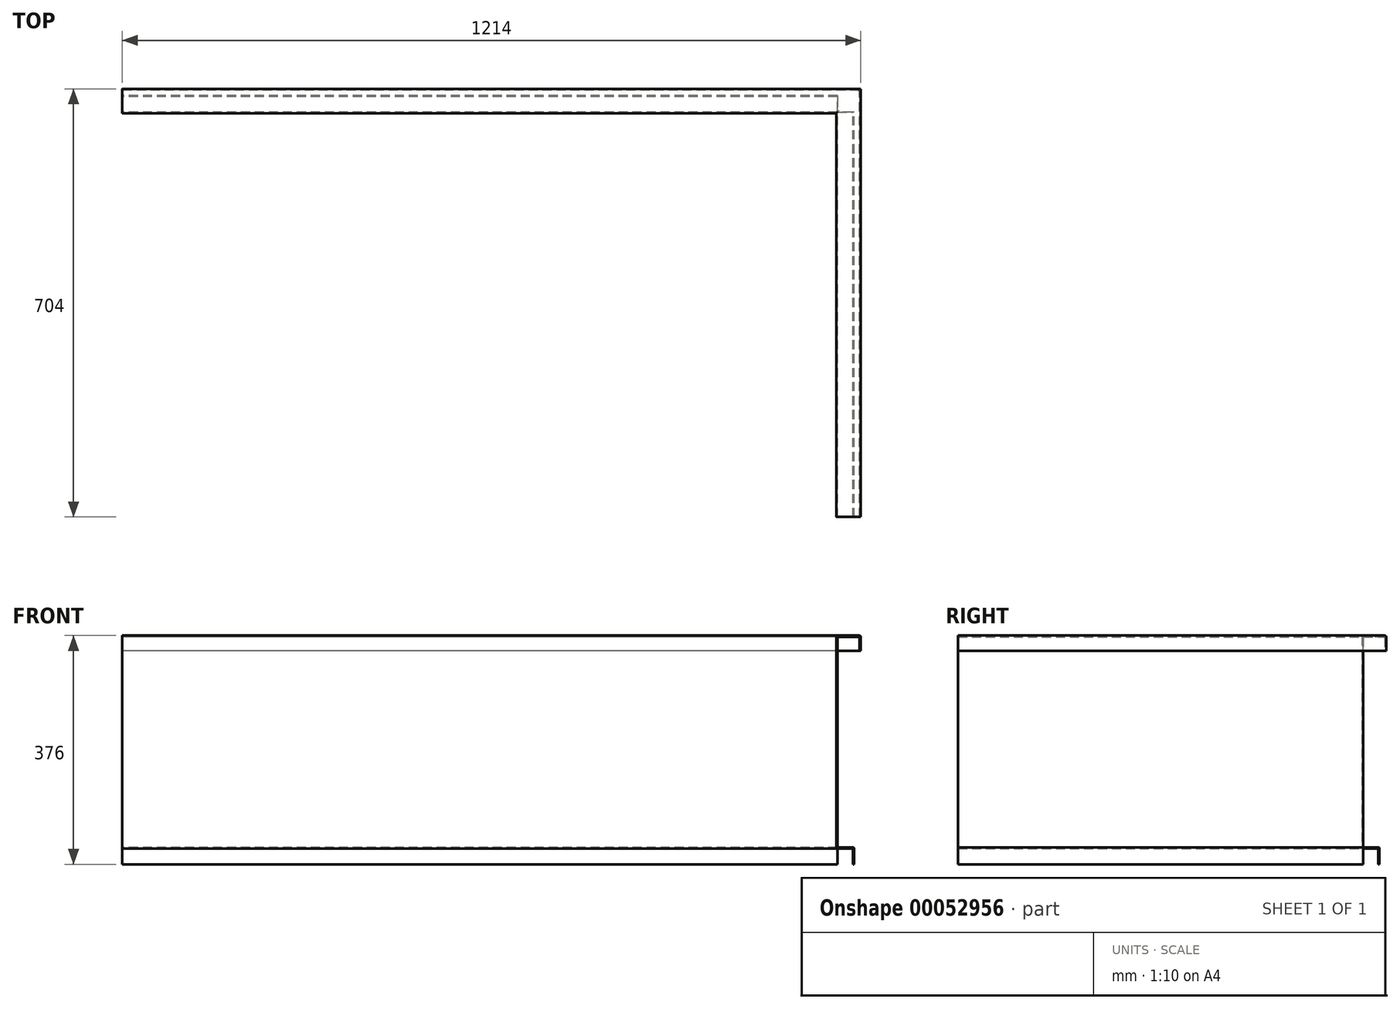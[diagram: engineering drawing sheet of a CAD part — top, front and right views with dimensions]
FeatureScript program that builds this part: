
annotation { "Feature Type Name" : "Feature", "Feature Type Description" : "" }
export const myFeature = defineFeature(function(context is Context, id is Id, definition is map)
    precondition{}
    {
        {
            var Q0;
            Q0=qCreatedBy(makeId("Front.planeOp"),FACE);
            var sketch = newSketch(context, id + "F0", { "sketchPlane" : qUnion([Q0])});
            skLineSegment(sketch, "E0", {"start": v(38, -25) * mm, "end": v(38, -2) * mm});
            skLineSegment(sketch, "E1", {"start": v(38, -2) * mm, "end": v(2, -2) * mm});
            skLineSegment(sketch, "E2", {"start": v(2, -2) * mm, "end": v(2, -348) * mm});
            skLineSegment(sketch, "E3", {"start": v(2, -348) * mm, "end": v(29, -348) * mm});
            skLineSegment(sketch, "E4", {"start": v(29, -348) * mm, "end": v(29, -376) * mm});
            skLineSegment(sketch, "E5.0", {"start": v(27, -350) * mm, "end": v(27, -376) * mm});
            skLineSegment(sketch, "E5.1", {"start": v(40, -25) * mm, "end": v(40, 0) * mm});
            skLineSegment(sketch, "E5.2", {"start": v(40, 0) * mm, "end": v(0, 0) * mm});
            skLineSegment(sketch, "E5.3", {"start": v(0, 0) * mm, "end": v(0, -350) * mm});
            skLineSegment(sketch, "E5.4", {"start": v(0, -350) * mm, "end": v(27, -350) * mm});
            skLineSegment(sketch, "E6", {"start": v(27, -376) * mm, "end": v(29, -376) * mm});
            skLineSegment(sketch, "E7", {"start": v(38, -25) * mm, "end": v(40, -25) * mm});
            skSolve(sketch);
        }
        {
            var Q0;
            Q0=qCreatedBy(makeId("Top.planeOp"),FACE);
            var sketch = newSketch(context, id + "F1", { "sketchPlane" : qUnion([Q0])});
            skLineSegment(sketch, "E8", {"start": v(0, 0) * mm, "end": v(0, 664) * mm});
            skLineSegment(sketch, "E9", {"start": v(0, 664) * mm, "end": v(-1174, 664) * mm});
            skSolve(sketch);
        }
        {
            var Q0;
            Q0 = qSketchRegion(id + "F0", true);
            var Q1;
            Q1 = qConstructionFilter(qBodyType(qCreatedBy(id + "F1" ,EDGE), BodyType.WIRE), ConstructionObject.NO);
            sweep(context, id + "F2", {"profiles" : qUnion([Q0]), "path" : qUnion([Q1])});
        }
        {
            var Q0;
            Q0=makeQuery(id+"F2.opSweep","SWEPT_FACE",FACE,{"disambiguationData":[OSD([sQuery(id+"F0.wireOp",EDGE,"E3"),sQuery(id+"F1.wireOp",EDGE,"E8")])]});
            var sketch = newSketch(context, id + "F3", { "sketchPlane" : qUnion([Q0])});
            skLineSegment(sketch, "E10.bottom", {"start": v(2, 666) * mm, "end": v(29, 666) * mm});
            skLineSegment(sketch, "E10.top", {"start": v(2, 693) * mm, "end": v(29, 693) * mm});
            skLineSegment(sketch, "E10.left", {"start": v(2, 666) * mm, "end": v(2, 693) * mm});
            skLineSegment(sketch, "E10.right", {"start": v(29, 666) * mm, "end": v(29, 693) * mm});
            skSolve(sketch);
        }
        {
            var Q0;
            Q0 = qSketchRegion(id + "F3", true);
            extrude(context, id + "F4", {"entities" : qUnion([Q0]), "operationType" : NewBodyOperationType.REMOVE, "oppositeDirection" : true, "depth" : 30 * mm});
        }
        {
            var Q0;
            Q0=makeQuery(id+"F2.opSweep","SWEPT_EDGE",EDGE,{"disambiguationData":[OSD([sQuery(id+"F0.wireOp",EDGE,"E3"),sQuery(id+"F0.wireOp",EDGE,"E4"),sQuery(id+"F1.wireOp",EDGE,"E9")])]});
            var Q1;
            Q1=makeQuery(id+"F2.opSweep","SWEPT_EDGE",EDGE,{"disambiguationData":[OSD([sQuery(id+"F0.wireOp",EDGE,"E2"),sQuery(id+"F0.wireOp",EDGE,"E3"),sQuery(id+"F1.wireOp",EDGE,"E9")])]});
            var Q2;
            Q2=makeQuery(id+"F2.opSweep","SWEPT_EDGE",EDGE,{"disambiguationData":[OSD([sQuery(id+"F0.wireOp",EDGE,"E5.1"),sQuery(id+"F0.wireOp",EDGE,"E5.2"),sQuery(id+"F1.wireOp",EDGE,"E9")])]});
            var Q3;
            Q3=makeQuery(id+"F2.opSweep","SWEPT_EDGE",EDGE,{"disambiguationData":[OSD([sQuery(id+"F0.wireOp",EDGE,"E5.2"),sQuery(id+"F0.wireOp",EDGE,"E5.3"),sQuery(id+"F1.wireOp",EDGE,"E9")])]});
            var Q4;
            Q4=makeQuery(id+"F2.opSweep","SWEPT_EDGE",EDGE,{"disambiguationData":[OSD([sQuery(id+"F0.wireOp",EDGE,"E5.3"),sQuery(id+"F0.wireOp",EDGE,"E5.4"),sQuery(id+"F1.wireOp",EDGE,"E9")])]});
            var Q5;
            Q5=makeQuery(id+"F2.opSweep","SWEPT_EDGE",EDGE,{"disambiguationData":[OSD([sQuery(id+"F0.wireOp",EDGE,"E5.0"),sQuery(id+"F0.wireOp",EDGE,"E5.4"),sQuery(id+"F1.wireOp",EDGE,"E9")])]});
            var Q6;
            Q6=makeQuery(id+"F2.opSweep","SWEPT_EDGE",EDGE,{"disambiguationData":[OSD([sQuery(id+"F0.wireOp",EDGE,"E1"),sQuery(id+"F0.wireOp",EDGE,"E2"),sQuery(id+"F1.wireOp",EDGE,"E9")])]});
            var Q7;
            Q7=makeQuery(id+"F2.opSweep","SWEPT_EDGE",EDGE,{"disambiguationData":[OSD([sQuery(id+"F0.wireOp",EDGE,"E0"),sQuery(id+"F0.wireOp",EDGE,"E1"),sQuery(id+"F1.wireOp",EDGE,"E9")])]});
            var Q8;
            Q8=makeQuery(id+"F2.opSweep","SWEPT_EDGE",EDGE,{"disambiguationData":[OSD([sQuery(id+"F0.wireOp",EDGE,"E5.1"),sQuery(id+"F0.wireOp",EDGE,"E5.2"),sQuery(id+"F1.wireOp",EDGE,"E8")])]});
            var Q9;
            Q9=makeQuery(id+"F2.opSweep","SWEPT_EDGE",EDGE,{"disambiguationData":[OSD([sQuery(id+"F0.wireOp",EDGE,"E5.2"),sQuery(id+"F0.wireOp",EDGE,"E5.3"),sQuery(id+"F1.wireOp",EDGE,"E8")])]});
            var Q10;
            Q10=makeQuery(id+"F2.opSweep","SWEPT_EDGE",EDGE,{"disambiguationData":[OSD([sQuery(id+"F0.wireOp",EDGE,"E5.3"),sQuery(id+"F0.wireOp",EDGE,"E5.4"),sQuery(id+"F1.wireOp",EDGE,"E8")])]});
            var Q11;
            Q11=makeQuery(id+"F2.opSweep","SWEPT_EDGE",EDGE,{"disambiguationData":[OSD([sQuery(id+"F0.wireOp",EDGE,"E5.0"),sQuery(id+"F0.wireOp",EDGE,"E5.4"),sQuery(id+"F1.wireOp",EDGE,"E8")])]});
            var Q12;
            Q12=makeQuery(id+"F2.opSweep","SWEPT_EDGE",EDGE,{"disambiguationData":[OSD([sQuery(id+"F0.wireOp",EDGE,"E3"),sQuery(id+"F0.wireOp",EDGE,"E4"),sQuery(id+"F1.wireOp",EDGE,"E8")])]});
            var Q13;
            Q13=makeQuery(id+"F2.opSweep","SWEPT_EDGE",EDGE,{"disambiguationData":[OSD([sQuery(id+"F0.wireOp",EDGE,"E0"),sQuery(id+"F0.wireOp",EDGE,"E1"),sQuery(id+"F1.wireOp",EDGE,"E8")])]});
            var Q14;
            Q14=makeQuery(id+"F2.opSweep","SWEPT_EDGE",EDGE,{"disambiguationData":[OSD([sQuery(id+"F0.wireOp",EDGE,"E1"),sQuery(id+"F0.wireOp",EDGE,"E2"),sQuery(id+"F1.wireOp",EDGE,"E8")])]});
            fillet(context, id + "F5", {"entities" : qUnion([Q0, Q1, Q2, Q3, Q4, Q5, Q6, Q7, Q8, Q9, Q10, Q11, Q12, Q13, Q14]), "radius" : 2 * mm, "tangentPropagation" : true, "allowEdgeOverflow" : false});
        }
    });
